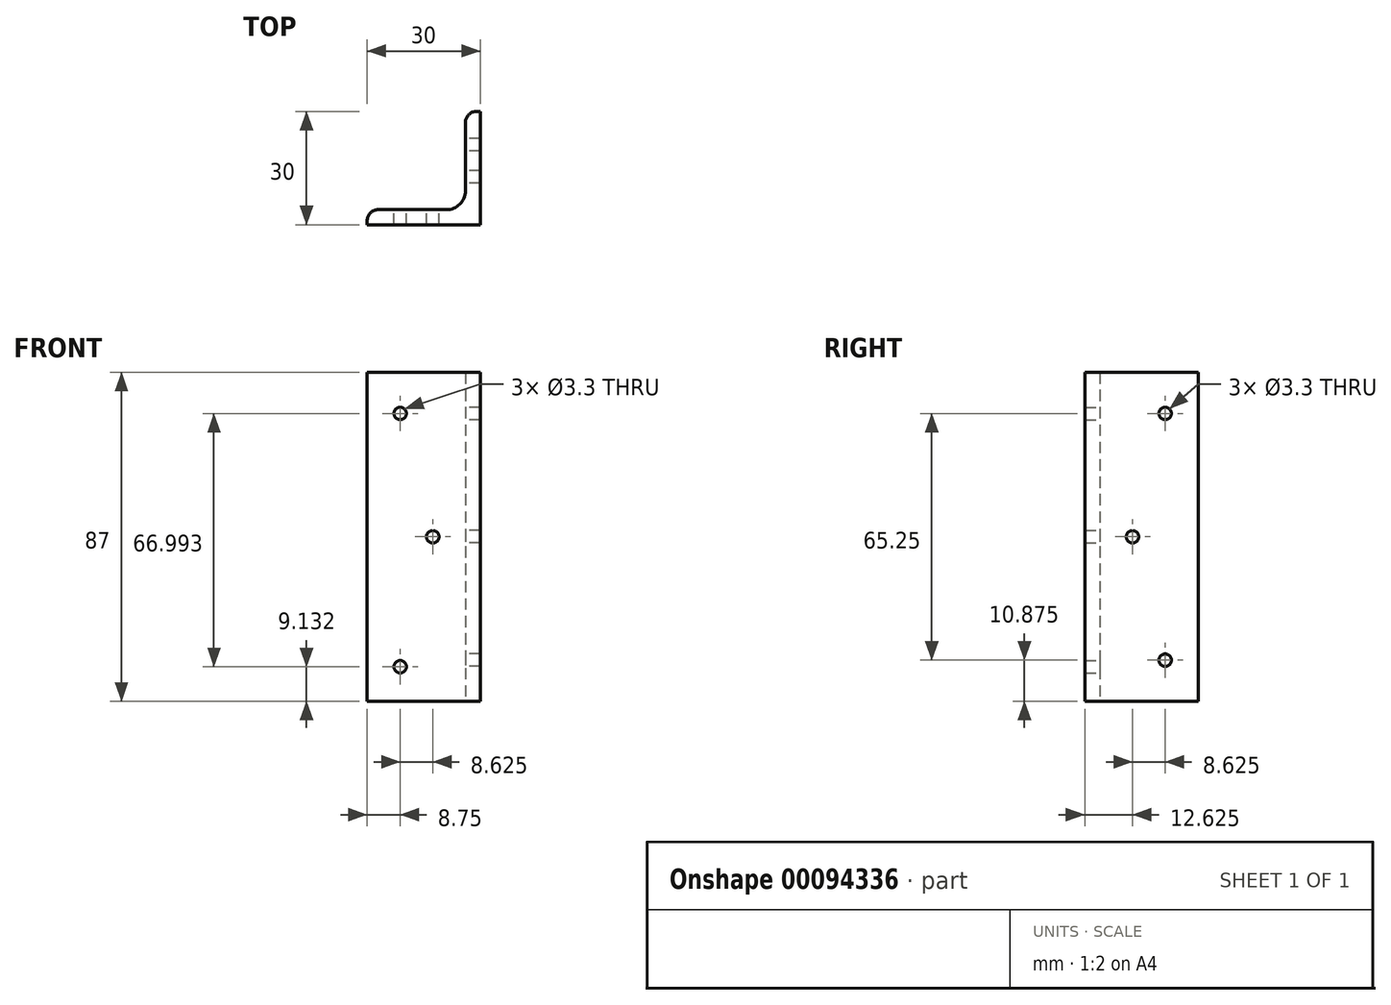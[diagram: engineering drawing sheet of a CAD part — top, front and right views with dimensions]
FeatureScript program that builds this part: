
annotation { "Feature Type Name" : "Feature", "Feature Type Description" : "" }
export const myFeature = defineFeature(function(context is Context, id is Id, definition is map)
    precondition{}
    {
        {
            var Q0;
            Q0=qCreatedBy(makeId("Top.planeOp"),FACE);
            var sketch = newSketch(context, id + "F0", { "sketchPlane" : qUnion([Q0])});
            skLineSegment(sketch, "E0.bottom", {"start": v(3, 0) * mm, "end": v(30, 0) * mm});
            skLineSegment(sketch, "E0.top", {"start": v(0, -4) * mm, "end": v(30, -4) * mm});
            skLineSegment(sketch, "E0.left", {"start": v(0, -3) * mm, "end": v(0, -4) * mm});
            skLineSegment(sketch, "E0.right", {"start": v(30, 0) * mm, "end": v(30, -4) * mm});
            skLineSegment(sketch, "E1.top", {"start": v(30, 26) * mm, "end": v(29, 26) * mm});
            skLineSegment(sketch, "E1.left", {"start": v(30, 0) * mm, "end": v(30, 26) * mm});
            skLineSegment(sketch, "E1.right", {"start": v(26, 0) * mm, "end": v(26, 23) * mm});
            skPoint(sketch, "E2.visualSharp", {"position": v(26, 26) * mm});
            skArc(sketch, "E2.filletArc", {"start": v(29, 26) * mm, "mid": v(26.88, 25.12) * mm, "end": v(26, 23) * mm});
            skPoint(sketch, "E3.visualSharp", {"position": v(0, 0) * mm});
            skArc(sketch, "E3.filletArc", {"start": v(3, 0) * mm, "mid": v(0.88, -0.88) * mm, "end": v(0, -3) * mm});
            skSolve(sketch);
        }
        {
            var Q0;
            Q0=makeQuery(id+"F0.imprint","IMPRINT",FACE,{"disambiguationData":[TD([[makeQuery(id+"F0.imprint","IMPRINT",EDGE,{"derivedFrom":sQuery(id+"F0.wireOp",EDGE,"E1.top")}),1.0]])]});
            var Q1;
            Q1=makeQuery(id+"F0.imprint","IMPRINT",FACE,{"disambiguationData":[TD([[makeQuery(id+"F0.imprint","IMPRINT",EDGE,{"derivedFrom":sQuery(id+"F0.wireOp",EDGE,"E0.top")}),1.0]])]});
            extrude(context, id + "F1", {"entities" : qUnion([Q0, Q1]), "depth" : 87 * mm});
        }
        {
            var Q0;
            Q0=makeQuery(id+"F1.opExtrude","SWEPT_FACE",FACE,{"disambiguationData":[OSD([sQuery(id+"F0.wireOp",EDGE,"E1.right")])]});
            var sketch = newSketch(context, id + "F2", { "sketchPlane" : qUnion([Q0])});
            skLineSegment(sketch, "E4", {"start": v(-11.5, 0) * mm, "end": v(-11.5, 87) * mm});
            skLineSegment(sketch, "E5", {"start": v(-11.5, 87) * mm, "end": v(-23, 87) * mm});
            skLineSegment(sketch, "E6", {"start": v(-23, 87) * mm, "end": v(-17.25, 87) * mm});
            skLineSegment(sketch, "E7", {"start": v(-17.25, 87) * mm, "end": v(-17.25, 0) * mm});
            skLineSegment(sketch, "E8", {"start": v(-17.25, 0) * mm, "end": v(-17.25, 43.5) * mm});
            skLineSegment(sketch, "E9", {"start": v(-17.25, 43.5) * mm, "end": v(-17.25, 21.75) * mm});
            skLineSegment(sketch, "E10", {"start": v(-17.25, 43.5) * mm, "end": v(-17.25, 87) * mm});
            skLineSegment(sketch, "E11", {"start": v(-17.25, 65.25) * mm, "end": v(-17.25, 87) * mm});
            skLineSegment(sketch, "E12", {"start": v(-17.25, 0) * mm, "end": v(-17.25, 21.75) * mm});
            skPoint(sketch, "E13", {"position": v(-17.25, 76.12) * mm});
            skPoint(sketch, "E14", {"position": v(-17.25, 10.88) * mm});
            skLineSegment(sketch, "E15", {"start": v(-17.25, 43.5) * mm, "end": v(0, 43.5) * mm});
            skLineSegment(sketch, "E16", {"start": v(0, 43.5) * mm, "end": v(-8.62, 43.5) * mm});
            skSolve(sketch);
        }
        {
            var Q0;
            Q0=makeQuery(id+"F1.opExtrude","SWEPT_FACE",FACE,{"disambiguationData":[OSD([sQuery(id+"F0.wireOp",EDGE,"E0.bottom")])]});
            var sketch = newSketch(context, id + "F3", { "sketchPlane" : qUnion([Q0])});
            skLineSegment(sketch, "E17", {"start": v(-26, 0) * mm, "end": v(-14.5, 0) * mm});
            skLineSegment(sketch, "E18", {"start": v(-14.5, 0) * mm, "end": v(-14.5, 87) * mm});
            skLineSegment(sketch, "E19", {"start": v(-14.5, 87) * mm, "end": v(-3, 87) * mm});
            skLineSegment(sketch, "E20", {"start": v(-3, 87) * mm, "end": v(-8.75, 87) * mm});
            skLineSegment(sketch, "E21", {"start": v(-8.75, 87) * mm, "end": v(-8.75, 0) * mm});
            skLineSegment(sketch, "E22", {"start": v(-8.75, 0) * mm, "end": v(-8.75, 43.5) * mm});
            skLineSegment(sketch, "E23", {"start": v(-8.75, 43.5) * mm, "end": v(-8.75, 87) * mm});
            skLineSegment(sketch, "E24", {"start": v(-8.75, 65.25) * mm, "end": v(-8.75, 87) * mm});
            skPoint(sketch, "E25", {"position": v(-8.75, 76.12) * mm});
            skLineSegment(sketch, "E26", {"start": v(-8.75, 21.75) * mm, "end": v(-8.75, 0) * mm});
            skPoint(sketch, "E27", {"position": v(-8.75, 9.13) * mm});
            skLineSegment(sketch, "E28", {"start": v(-8.75, 43.5) * mm, "end": v(-26, 43.5) * mm});
            skLineSegment(sketch, "E29", {"start": v(-26, 43.5) * mm, "end": v(-17.37, 43.5) * mm});
            skPoint(sketch, "E30", {"position": v(-17.37, 43.5) * mm});
            skSolve(sketch);
        }
        {
            var Q0;
            Q0=sQuery(id+"F2.wireOp",VERTEX,"E14");
            var Q1;
            Q1=sQuery(id+"F2.wireOp",VERTEX,"E13");
            var Q2;
            Q2=sQuery(id+"F2.wireOp",VERTEX,"E16.end");
            var Q3;
            Q3=sQuery(id+"F3.wireOp",VERTEX,"E27");
            var Q4;
            Q4=sQuery(id+"F3.wireOp",VERTEX,"E30");
            var Q5;
            Q5=sQuery(id+"F3.wireOp",VERTEX,"E25");
            var Q6;
            Q6=makeQuery(id+"F1.opExtrude","SWEPT_BODY",BODY,{"disambiguationData":[OSD([sQuery(id+"F0.wireOp",EDGE,"E0.bottom"),sQuery(id+"F0.wireOp",EDGE,"E0.top"),sQuery(id+"F0.wireOp",EDGE,"E0.left"),sQuery(id+"F0.wireOp",EDGE,"E0.right"),sQuery(id+"F0.wireOp",EDGE,"E1.top"),sQuery(id+"F0.wireOp",EDGE,"E1.left"),sQuery(id+"F0.wireOp",EDGE,"E1.right"),sQuery(id+"F0.wireOp",EDGE,"E2.filletArc"),sQuery(id+"F0.wireOp",EDGE,"E3.filletArc")])]});
            hole(context, id + "F4", {"style" : HoleStyle.SIMPLE, "endStyle" : HoleEndStyle.THROUGH, "holeDiameter" : 3.3 * mm, "locations" : qUnion([Q0, Q1, Q2, Q3, Q4, Q5]), "scope" : qUnion([Q6]), "isTappedThrough" : true});
        }
        {
            var Q0;
            Q0=makeQuery(id+"F1.opExtrude","SWEPT_EDGE",EDGE,{"disambiguationData":[OSD([sQuery(id+"F0.wireOp",EDGE,"E0.bottom"),sQuery(id+"F0.wireOp",EDGE,"E1.right")])]});
            fillet(context, id + "F5", {"entities" : qUnion([Q0]), "radius" : 5 * mm, "tangentPropagation" : true, "allowEdgeOverflow" : false});
        }
    });
